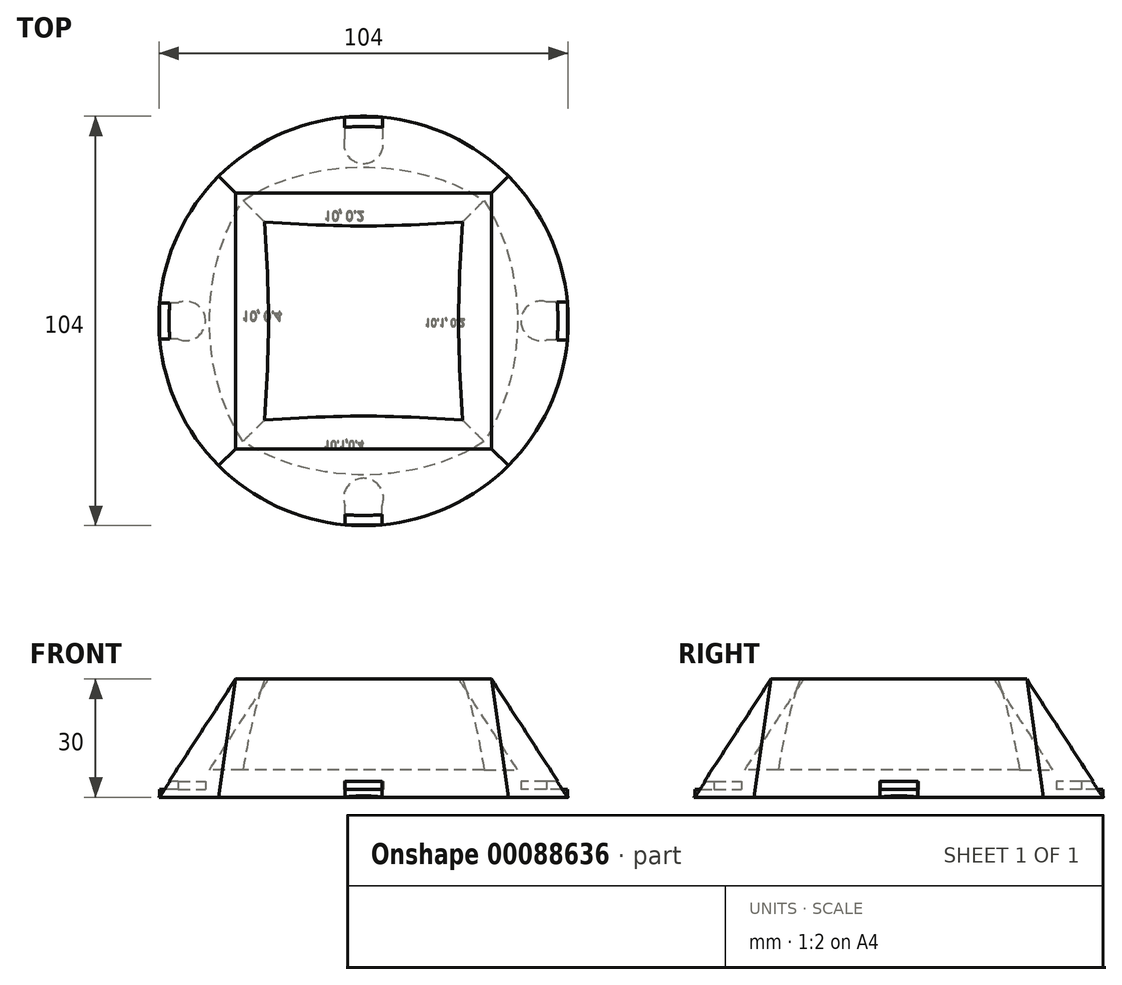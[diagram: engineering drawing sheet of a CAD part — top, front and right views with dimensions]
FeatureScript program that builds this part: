
annotation { "Feature Type Name" : "Feature", "Feature Type Description" : "" }
export const myFeature = defineFeature(function(context is Context, id is Id, definition is map)
    precondition{}
    {
        {
            var Q0;
            Q0=qCreatedBy(makeId("Top.planeOp"),FACE);
            var sketch = newSketch(context, id + "F0", { "sketchPlane" : qUnion([Q0])});
            skCircle(sketch, "E0", {"center": v(0, 0) * mm, "radius": 52 * mm});
            skSolve(sketch);
        }
        {
            var Q0;
            Q0=qCreatedBy(makeId("Top.planeOp"),FACE);
            cPlane(context, id + "F1", {"entities" : qUnion([Q0]), "cplaneType" : CPlaneType.OFFSET, "offset" : 30 * mm, "width" : 152.4 * mm, "height" : 152.4 * mm});
        }
        {
            var Q0;
            Q0=qCreatedBy(id+"F1.planeOp",FACE);
            var sketch = newSketch(context, id + "F2", { "sketchPlane" : qUnion([Q0])});
            skLineSegment(sketch, "E1.bottom", {"start": v(-32.5, -32.5) * mm, "end": v(32.5, -32.5) * mm});
            skLineSegment(sketch, "E1.top", {"start": v(-32.5, 32.5) * mm, "end": v(32.5, 32.5) * mm});
            skLineSegment(sketch, "E1.left", {"start": v(-32.5, -32.5) * mm, "end": v(-32.5, 32.5) * mm});
            skLineSegment(sketch, "E1.right", {"start": v(32.5, -32.5) * mm, "end": v(32.5, 32.5) * mm});
            skPoint(sketch, "E1.middle", {"position": v(0, 0) * mm});
            skSolve(sketch);
        }
        {
            var Q0;
            Q0=makeQuery(id+"F2.imprint","IMPRINT",FACE,{"disambiguationData":[TD([[makeQuery(id+"F2.imprint","IMPRINT",EDGE,{"derivedFrom":sQuery(id+"F2.wireOp",EDGE,"E1.bottom")}),1.0]])]});
            var Q1;
            Q1=makeQuery(id+"F0.imprint","IMPRINT",FACE,{"disambiguationData":[TD([[makeQuery(id+"F0.imprint","IMPRINT",EDGE,{"derivedFrom":sQuery(id+"F0.wireOp",EDGE,"E0")}),1.0]])]});
            loft(context, id + "F3", {"sheetProfilesArray" : [{ "sheetProfileEntities" : qUnion([Q0]) }, { "sheetProfileEntities" : qUnion([Q1]) }]});
        }
        {
            var Q0;
            Q0=makeQuery(id+"F3.opLoft","CAP_FACE",FACE,{"disambiguationData":[OSD([makeQuery(id+"F2.imprint","IMPRINT",FACE,{"disambiguationData":[TD([[makeQuery(id+"F2.imprint","IMPRINT",EDGE,{"derivedFrom":sQuery(id+"F2.wireOp",EDGE,"E1.bottom")}),1.0]])]})])],"isStart":true});
            shell(context, id + "F4", {"entities" : qUnion([Q0]), "thickness" : 7 * mm});
        }
        {
            var Q0;
            Q0=makeQuery(id+"F3.opLoft","CAP_FACE",FACE,{"disambiguationData":[OSD([makeQuery(id+"F0.imprint","IMPRINT",FACE,{"disambiguationData":[TD([[makeQuery(id+"F0.imprint","IMPRINT",EDGE,{"derivedFrom":sQuery(id+"F0.wireOp",EDGE,"E0")}),1.0]])]})])],"isStart":true});
            var sketch = newSketch(context, id + "F5", { "sketchPlane" : qUnion([Q0])});
            skPoint(sketch, "E2.middle", {"position": v(0, 0) * mm});
            skCircle(sketch, "E3", {"center": v(0, 45) * mm, "radius": 5.05 * mm});
            skCircle(sketch, "E4", {"center": v(-45.15, 0) * mm, "radius": 5 * mm});
            skCircle(sketch, "E5", {"center": v(0, -45) * mm, "radius": 5 * mm});
            skCircle(sketch, "E6", {"center": v(45.06, 0) * mm, "radius": 5.05 * mm});
            skLineSegment(sketch, "E7.bottom", {"start": v(-45.08, -4.6) * mm, "end": v(-51.8, -4.6) * mm});
            skLineSegment(sketch, "E7.top", {"start": v(-45.08, 4.6) * mm, "end": v(-51.8, 4.6) * mm});
            skLineSegment(sketch, "E7.left", {"start": v(-45.08, -4.6) * mm, "end": v(-45.08, 4.6) * mm});
            skLineSegment(sketch, "E7.right", {"start": v(-51.8, -4.6) * mm, "end": v(-51.8, 4.6) * mm});
            skLineSegment(sketch, "E8.bottom", {"start": v(-4.8, -51.78) * mm, "end": v(4.8, -51.78) * mm});
            skLineSegment(sketch, "E8.top", {"start": v(-4.8, -45) * mm, "end": v(4.8, -45) * mm});
            skLineSegment(sketch, "E8.left", {"start": v(-4.8, -51.78) * mm, "end": v(-4.8, -45) * mm});
            skLineSegment(sketch, "E8.right", {"start": v(4.8, -51.78) * mm, "end": v(4.8, -45) * mm});
            skLineSegment(sketch, "E9.bottom", {"start": v(51.77, -4.85) * mm, "end": v(45.06, -4.85) * mm});
            skLineSegment(sketch, "E9.top", {"start": v(51.77, 4.85) * mm, "end": v(45.06, 4.85) * mm});
            skLineSegment(sketch, "E9.left", {"start": v(51.77, -4.85) * mm, "end": v(51.77, 4.85) * mm});
            skLineSegment(sketch, "E9.right", {"start": v(45.06, -4.85) * mm, "end": v(45.06, 4.85) * mm});
            skLineSegment(sketch, "E10.bottom", {"start": v(4.65, 51.8) * mm, "end": v(-4.65, 51.8) * mm});
            skLineSegment(sketch, "E10.top", {"start": v(4.65, 45) * mm, "end": v(-4.65, 45) * mm});
            skLineSegment(sketch, "E10.left", {"start": v(4.65, 51.8) * mm, "end": v(4.65, 45) * mm});
            skLineSegment(sketch, "E10.right", {"start": v(-4.65, 51.8) * mm, "end": v(-4.65, 45) * mm});
            skSolve(sketch);
        }
        {
            var Q0;
            {var subQ5=sQuery(id+"F5.wireOp",EDGE,"P9WS4JfC-322q-SWWd-xQKO-A7a6ZTN9kQBs.top");Q0=makeQuery(id+"F5.imprint","IMPRINT",FACE,{"disambiguationData":[TD([[makeQuery(id+"F5.imprint","IMPRINT",EDGE,{"derivedFrom":subQ5}),-1.0]])]});}
            var Q1;
            {var subQ5=sQuery(id+"F5.wireOp",EDGE,"P9WS4JfC-322q-SWWd-xQKO-A7a6ZTN9kQBs.top");Q1=makeQuery(id+"F5.imprint","IMPRINT",FACE,{"disambiguationData":[TD([[makeQuery(id+"F5.imprint","IMPRINT",EDGE,{"derivedFrom":subQ5}),1.0]])]});}
            var Q2;
            {var subQ0=sQuery(id+"F5.wireOp",EDGE,"P9WS4JfC-322q-SWWd-xQKO-A7a6ZTN9kQBs.left");var subQ1=sQuery(id+"F5.wireOp",EDGE,"E3");var subQ2=makeQuery(id+"F5.imprint","INTERSECT",VERTEX,{"derivedFrom":[subQ1,subQ0]});Q2=makeQuery(id+"F5.imprint","IMPRINT",FACE,{"disambiguationData":[TD([[makeQuery(id+"F5.imprint","IMPRINT",EDGE,{"disambiguationData":[TD([[subQ2,1.0]])],"derivedFrom":subQ1}),1.0]])]});}
            var Q3;
            {var subQ0=sQuery(id+"F5.wireOp",EDGE,"P9WS4JfC-322q-SWWd-xQKO-A7a6ZTN9kQBs.right");var subQ1=sQuery(id+"F5.wireOp",EDGE,"E3");var subQ2=makeQuery(id+"F5.imprint","INTERSECT",VERTEX,{"derivedFrom":[subQ1,subQ0]});Q3=makeQuery(id+"F5.imprint","IMPRINT",FACE,{"disambiguationData":[TD([[makeQuery(id+"F5.imprint","IMPRINT",EDGE,{"disambiguationData":[TD([[subQ2,-1.0]])],"derivedFrom":subQ1}),1.0]])]});}
            var Q4;
            {var subQ0=sQuery(id+"F5.wireOp",EDGE,"P9WS4JfC-322q-SWWd-xQKO-A7a6ZTN9kQBs.right");var subQ1=sQuery(id+"F5.wireOp",EDGE,"E3");var subQ2=makeQuery(id+"F5.imprint","INTERSECT",VERTEX,{"derivedFrom":[subQ1,subQ0]});Q4=makeQuery(id+"F5.imprint","IMPRINT",FACE,{"disambiguationData":[TD([[makeQuery(id+"F5.imprint","IMPRINT",EDGE,{"disambiguationData":[TD([[subQ2,1.0]])],"derivedFrom":subQ1}),-1.0]])]});}
            var Q5;
            {var subQ0=sQuery(id+"F5.wireOp",EDGE,"P9WS4JfC-322q-SWWd-xQKO-A7a6ZTN9kQBs.bottom");Q5=makeQuery(id+"F5.imprint","IMPRINT",FACE,{"disambiguationData":[TD([[makeQuery(id+"F5.imprint","IMPRINT",EDGE,{"derivedFrom":subQ0}),1.0]])]});}
            var Q6;
            {var subQ5=sQuery(id+"F5.wireOp",EDGE,"qYHTTBHr-f0L7-UdLb-VUg3-aonPYJzoOcQr.right");Q6=makeQuery(id+"F5.imprint","IMPRINT",FACE,{"disambiguationData":[TD([[makeQuery(id+"F5.imprint","IMPRINT",EDGE,{"derivedFrom":subQ5}),-1.0]])]});}
            var Q7;
            {var subQ5=sQuery(id+"F5.wireOp",EDGE,"qYHTTBHr-f0L7-UdLb-VUg3-aonPYJzoOcQr.right");Q7=makeQuery(id+"F5.imprint","IMPRINT",FACE,{"disambiguationData":[TD([[makeQuery(id+"F5.imprint","IMPRINT",EDGE,{"derivedFrom":subQ5}),1.0]])]});}
            var Q8;
            {var subQ0=sQuery(id+"F5.wireOp",EDGE,"qYHTTBHr-f0L7-UdLb-VUg3-aonPYJzoOcQr.left");Q8=makeQuery(id+"F5.imprint","IMPRINT",FACE,{"disambiguationData":[TD([[makeQuery(id+"F5.imprint","IMPRINT",EDGE,{"derivedFrom":subQ0}),-1.0]])]});}
            var Q9;
            {var subQ0=sQuery(id+"F5.wireOp",EDGE,"qYHTTBHr-f0L7-UdLb-VUg3-aonPYJzoOcQr.top");var subQ1=sQuery(id+"F5.wireOp",EDGE,"E4");var subQ2=makeQuery(id+"F5.imprint","INTERSECT",VERTEX,{"derivedFrom":[subQ1,subQ0]});Q9=makeQuery(id+"F5.imprint","IMPRINT",FACE,{"disambiguationData":[TD([[makeQuery(id+"F5.imprint","IMPRINT",EDGE,{"disambiguationData":[TD([[subQ2,-1.0]])],"derivedFrom":subQ1}),-1.0]])]});}
            var Q10;
            {var subQ0=sQuery(id+"F5.wireOp",EDGE,"qYHTTBHr-f0L7-UdLb-VUg3-aonPYJzoOcQr.top");var subQ1=sQuery(id+"F5.wireOp",EDGE,"E4");var subQ2=makeQuery(id+"F5.imprint","INTERSECT",VERTEX,{"derivedFrom":[subQ1,subQ0]});Q10=makeQuery(id+"F5.imprint","IMPRINT",FACE,{"disambiguationData":[TD([[makeQuery(id+"F5.imprint","IMPRINT",EDGE,{"disambiguationData":[TD([[subQ2,1.0]])],"derivedFrom":subQ1}),1.0]])]});}
            var Q11;
            {var subQ0=sQuery(id+"F5.wireOp",EDGE,"qYHTTBHr-f0L7-UdLb-VUg3-aonPYJzoOcQr.bottom");var subQ1=sQuery(id+"F5.wireOp",EDGE,"E4");var subQ2=makeQuery(id+"F5.imprint","INTERSECT",VERTEX,{"derivedFrom":[subQ1,subQ0]});Q11=makeQuery(id+"F5.imprint","IMPRINT",FACE,{"disambiguationData":[TD([[makeQuery(id+"F5.imprint","IMPRINT",EDGE,{"disambiguationData":[TD([[subQ2,-1.0]])],"derivedFrom":subQ1}),1.0]])]});}
            var Q12;
            {var subQ5=sQuery(id+"F5.wireOp",EDGE,"R9PYM033-Zrmn-WzrL-YFal-hppJ3v3tyKf0.top");Q12=makeQuery(id+"F5.imprint","IMPRINT",FACE,{"disambiguationData":[TD([[makeQuery(id+"F5.imprint","IMPRINT",EDGE,{"derivedFrom":subQ5}),-1.0]])]});}
            var Q13;
            {var subQ5=sQuery(id+"F5.wireOp",EDGE,"R9PYM033-Zrmn-WzrL-YFal-hppJ3v3tyKf0.top");Q13=makeQuery(id+"F5.imprint","IMPRINT",FACE,{"disambiguationData":[TD([[makeQuery(id+"F5.imprint","IMPRINT",EDGE,{"derivedFrom":subQ5}),1.0]])]});}
            var Q14;
            {var subQ0=sQuery(id+"F5.wireOp",EDGE,"R9PYM033-Zrmn-WzrL-YFal-hppJ3v3tyKf0.right");var subQ1=sQuery(id+"F5.wireOp",EDGE,"E5");var subQ2=makeQuery(id+"F5.imprint","INTERSECT",VERTEX,{"derivedFrom":[subQ1,subQ0]});Q14=makeQuery(id+"F5.imprint","IMPRINT",FACE,{"disambiguationData":[TD([[makeQuery(id+"F5.imprint","IMPRINT",EDGE,{"disambiguationData":[TD([[subQ2,-1.0]])],"derivedFrom":subQ1}),-1.0]])]});}
            var Q15;
            {var subQ0=sQuery(id+"F5.wireOp",EDGE,"R9PYM033-Zrmn-WzrL-YFal-hppJ3v3tyKf0.bottom");Q15=makeQuery(id+"F5.imprint","IMPRINT",FACE,{"disambiguationData":[TD([[makeQuery(id+"F5.imprint","IMPRINT",EDGE,{"derivedFrom":subQ0}),-1.0]])]});}
            var Q16;
            {var subQ0=sQuery(id+"F5.wireOp",EDGE,"lRnhWXqZ-bgOf-f2S0-9nqJ-WSJoJMWuuvkY.bottom");var subQ1=sQuery(id+"F5.wireOp",EDGE,"E5");var subQ2=makeQuery(id+"F5.imprint","INTERSECT",VERTEX,{"disambiguationData":[OD(0.0)],"derivedFrom":[subQ1,subQ0]});Q16=makeQuery(id+"F5.imprint","IMPRINT",FACE,{"disambiguationData":[TD([[makeQuery(id+"F5.imprint","IMPRINT",EDGE,{"disambiguationData":[TD([[subQ2,-1.0]])],"derivedFrom":subQ1}),1.0]])]});}
            var Q17;
            {var subQ0=sQuery(id+"F5.wireOp",EDGE,"lRnhWXqZ-bgOf-f2S0-9nqJ-WSJoJMWuuvkY.bottom");var subQ1=sQuery(id+"F5.wireOp",EDGE,"E5");var subQ2=makeQuery(id+"F5.imprint","INTERSECT",VERTEX,{"disambiguationData":[OD(1.0)],"derivedFrom":[subQ1,subQ0]});Q17=makeQuery(id+"F5.imprint","IMPRINT",FACE,{"disambiguationData":[TD([[makeQuery(id+"F5.imprint","IMPRINT",EDGE,{"disambiguationData":[TD([[subQ2,1.0]])],"derivedFrom":subQ1}),1.0]])]});}
            var Q18;
            {var subQ0=sQuery(id+"F5.wireOp",EDGE,"lRnhWXqZ-bgOf-f2S0-9nqJ-WSJoJMWuuvkY.bottom");var subQ1=sQuery(id+"F5.wireOp",EDGE,"E5");var subQ2=makeQuery(id+"F5.imprint","INTERSECT",VERTEX,{"disambiguationData":[OD(1.0)],"derivedFrom":[subQ1,subQ0]});Q18=makeQuery(id+"F5.imprint","IMPRINT",FACE,{"disambiguationData":[TD([[makeQuery(id+"F5.imprint","IMPRINT",EDGE,{"disambiguationData":[TD([[subQ2,-1.0]])],"derivedFrom":subQ1}),1.0]])]});}
            var Q19;
            {var subQ0=sQuery(id+"F5.wireOp",EDGE,"V6ln2MYC-XStS-GRJf-wB7O-48xDgtNBXDmb.left");var subQ1=sQuery(id+"F5.wireOp",EDGE,"GTJJYR7q-po6W-yFHW-cKz8-xLbWGjphPWbZ.top");var subQ2=makeQuery(id+"F5.imprint","INTERSECT",VERTEX,{"derivedFrom":[subQ1,subQ0]});Q19=makeQuery(id+"F5.imprint","IMPRINT",FACE,{"disambiguationData":[TD([[makeQuery(id+"F5.imprint","IMPRINT",EDGE,{"disambiguationData":[TD([[subQ2,1.0]])],"derivedFrom":subQ0}),-1.0]])]});}
            var Q20;
            {var subQ0=sQuery(id+"F5.wireOp",EDGE,"V6ln2MYC-XStS-GRJf-wB7O-48xDgtNBXDmb.bottom");var subQ1=sQuery(id+"F5.wireOp",EDGE,"E6");var subQ2=makeQuery(id+"F5.imprint","INTERSECT",VERTEX,{"derivedFrom":[subQ1,subQ0]});Q20=makeQuery(id+"F5.imprint","IMPRINT",FACE,{"disambiguationData":[TD([[makeQuery(id+"F5.imprint","IMPRINT",EDGE,{"disambiguationData":[TD([[subQ2,1.0]])],"derivedFrom":subQ1}),1.0]])]});}
            var Q21;
            {var subQ0=sQuery(id+"F5.wireOp",EDGE,"GTJJYR7q-po6W-yFHW-cKz8-xLbWGjphPWbZ.bottom");var subQ1=sQuery(id+"F5.wireOp",EDGE,"E6");var subQ2=makeQuery(id+"F5.imprint","INTERSECT",VERTEX,{"derivedFrom":[subQ1,subQ0]});Q21=makeQuery(id+"F5.imprint","IMPRINT",FACE,{"disambiguationData":[TD([[makeQuery(id+"F5.imprint","IMPRINT",EDGE,{"disambiguationData":[TD([[subQ2,-1.0]])],"derivedFrom":subQ1}),1.0]])]});}
            var Q22;
            {var subQ1=sQuery(id+"F5.wireOp",EDGE,"E6");var subQ3=sQuery(id+"F5.wireOp",EDGE,"GTJJYR7q-po6W-yFHW-cKz8-xLbWGjphPWbZ.top");var subQ4=makeQuery(id+"F5.imprint","INTERSECT",VERTEX,{"disambiguationData":[OD(1.0)],"derivedFrom":[subQ1,subQ3]});Q22=makeQuery(id+"F5.imprint","IMPRINT",FACE,{"disambiguationData":[TD([[makeQuery(id+"F5.imprint","IMPRINT",EDGE,{"disambiguationData":[TD([[subQ4,-1.0]])],"derivedFrom":subQ3}),1.0]])]});}
            var Q23;
            {var subQ1=sQuery(id+"F5.wireOp",EDGE,"E6");var subQ3=sQuery(id+"F5.wireOp",EDGE,"GTJJYR7q-po6W-yFHW-cKz8-xLbWGjphPWbZ.top");var subQ4=makeQuery(id+"F5.imprint","INTERSECT",VERTEX,{"disambiguationData":[OD(0.0)],"derivedFrom":[subQ1,subQ3]});Q23=makeQuery(id+"F5.imprint","IMPRINT",FACE,{"disambiguationData":[TD([[makeQuery(id+"F5.imprint","IMPRINT",EDGE,{"disambiguationData":[TD([[subQ4,1.0]])],"derivedFrom":subQ3}),1.0]])]});}
            var Q24;
            {var subQ0=sQuery(id+"F5.wireOp",EDGE,"GTJJYR7q-po6W-yFHW-cKz8-xLbWGjphPWbZ.bottom");var subQ1=sQuery(id+"F5.wireOp",EDGE,"E6");var subQ2=makeQuery(id+"F5.imprint","INTERSECT",VERTEX,{"derivedFrom":[subQ1,subQ0]});Q24=makeQuery(id+"F5.imprint","IMPRINT",FACE,{"disambiguationData":[TD([[makeQuery(id+"F5.imprint","IMPRINT",EDGE,{"disambiguationData":[TD([[subQ2,1.0]])],"derivedFrom":subQ1}),1.0]])]});}
            var Q25;
            {var subQ0=sQuery(id+"F5.wireOp",EDGE,"V6ln2MYC-XStS-GRJf-wB7O-48xDgtNBXDmb.bottom");var subQ1=sQuery(id+"F5.wireOp",EDGE,"E6");var subQ2=makeQuery(id+"F5.imprint","INTERSECT",VERTEX,{"derivedFrom":[subQ1,subQ0]});Q25=makeQuery(id+"F5.imprint","IMPRINT",FACE,{"disambiguationData":[TD([[makeQuery(id+"F5.imprint","IMPRINT",EDGE,{"disambiguationData":[TD([[subQ2,1.0]])],"derivedFrom":subQ1}),-1.0]])]});}
            var Q26;
            {var subQ0=sQuery(id+"F5.wireOp",EDGE,"lRnhWXqZ-bgOf-f2S0-9nqJ-WSJoJMWuuvkY.bottom");var subQ1=sQuery(id+"F5.wireOp",EDGE,"E5");var subQ2=makeQuery(id+"F5.imprint","INTERSECT",VERTEX,{"disambiguationData":[OD(0.0)],"derivedFrom":[subQ1,subQ0]});Q26=makeQuery(id+"F5.imprint","IMPRINT",FACE,{"disambiguationData":[TD([[makeQuery(id+"F5.imprint","IMPRINT",EDGE,{"disambiguationData":[TD([[subQ2,1.0]])],"derivedFrom":subQ1}),1.0]])]});}
            extrude(context, id + "F6", {"entities" : qUnion([Q0, Q1, Q2, Q3, Q4, Q5, Q6, Q7, Q8, Q9, Q10, Q11, Q12, Q13, Q14, Q15, Q16, Q17, Q18, Q19, Q20, Q21, Q22, Q23, Q24, Q25, Q26]), "operationType" : NewBodyOperationType.REMOVE, "oppositeDirection" : true, "depth" : 4 * mm});
        }
        {
            var Q0;
            Q0 = qSketchRegion(id + "F0", true);
            extrude(context, id + "F7", {"entities" : qUnion([Q0]), "operationType" : NewBodyOperationType.REMOVE, "oppositeDirection" : true, "depth" : 25 * mm});
        }
        {
            var Q0;
            Q0 = qSketchRegion(id + "F5", true);
            extrude(context, id + "F8", {"entities" : qUnion([Q0]), "operationType" : NewBodyOperationType.ADD, "oppositeDirection" : true, "depth" : 2 * mm});
        }
        {
            var Q0;
            {var subQ25=sQuery(id+"F5.wireOp",EDGE,"E10.left");var subQ27=sQuery(id+"F5.wireOp",EDGE,"E3");var subQ28=makeQuery(id+"F5.imprint","INTERSECT",VERTEX,{"derivedFrom":[subQ27,subQ25]});Q0=makeQuery(id+"F5.imprint","IMPRINT",FACE,{"disambiguationData":[TD([[makeQuery(id+"F5.imprint","IMPRINT",EDGE,{"disambiguationData":[TD([[subQ28,1.0]])],"derivedFrom":subQ27}),-1.0]])]});}
            var sketch = newSketch(context, id + "F9", { "sketchPlane" : qUnion([Q0])});
            skText(sketch, "E11", { "text": "10, 0.2\n", "fontName": "OpenSans-Regular.ttf"});
            skText(sketch, "E12", { "text": "10, 0.4\n", "fontName": "OpenSans-Regular.ttf"});
            skText(sketch, "E13", { "text": "10.1,0.4\n", "fontName": "OpenSans-Regular.ttf"});
            skText(sketch, "E14", { "text": "10.1, 0.2", "fontName": "OpenSans-Regular.ttf"});
            const initialGuessF9  = {"E11": [-0.01, -0.02786, 1, 0, 0.0024], "E12": [-0.0308, -0.00237, 1, 0, 0.00237], "E13": [-0.01, 0.03051, 1, 0, 0.002], "E14": [0.01562, -0.00046, 1, 0, 0.00187]};
            skSetInitialGuess(sketch, initialGuessF9);
            skSolve(sketch);
        }
        {
            var Q0;
            Q0 = qSketchRegion(id + "F9", true);
            extrude(context, id + "F10", {"entities" : qUnion([Q0]), "operationType" : NewBodyOperationType.REMOVE, "oppositeDirection" : true, "depth" : 0.1 * mm});
        }
    });
